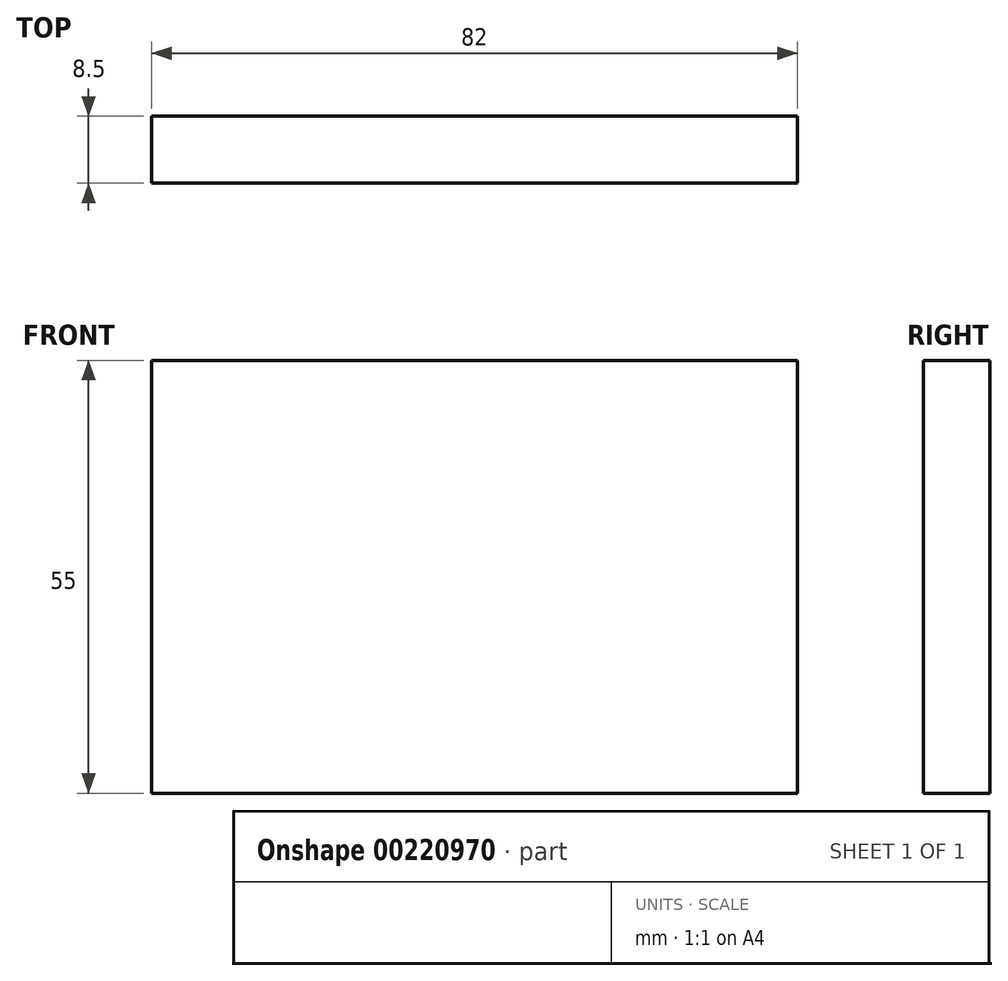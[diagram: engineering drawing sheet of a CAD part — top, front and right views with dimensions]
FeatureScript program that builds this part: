
annotation { "Feature Type Name" : "Feature", "Feature Type Description" : "" }
export const myFeature = defineFeature(function(context is Context, id is Id, definition is map)
    precondition{}
    {
        {
            var Q0;
            Q0=qCreatedBy(makeId("Front.planeOp"),FACE);
            var sketch = newSketch(context, id + "F0", { "sketchPlane" : qUnion([Q0])});
            skLineSegment(sketch, "E0", {"start": v(0, 0) * mm, "end": v(0, 55) * mm});
            skLineSegment(sketch, "E1", {"start": v(0, 55) * mm, "end": v(82, 55) * mm});
            skLineSegment(sketch, "E2", {"start": v(82, 55) * mm, "end": v(82, 0) * mm});
            skLineSegment(sketch, "E3", {"start": v(82, 0) * mm, "end": v(0, 0) * mm});
            skSolve(sketch);
        }
        {
            var Q0;
            Q0 = qSketchRegion(id + "F0", true);
            extrude(context, id + "F1", {"entities" : qUnion([Q0]), "depth" : 8.5 * mm, "offsetDistance" : 25 * mm});
        }
    });
